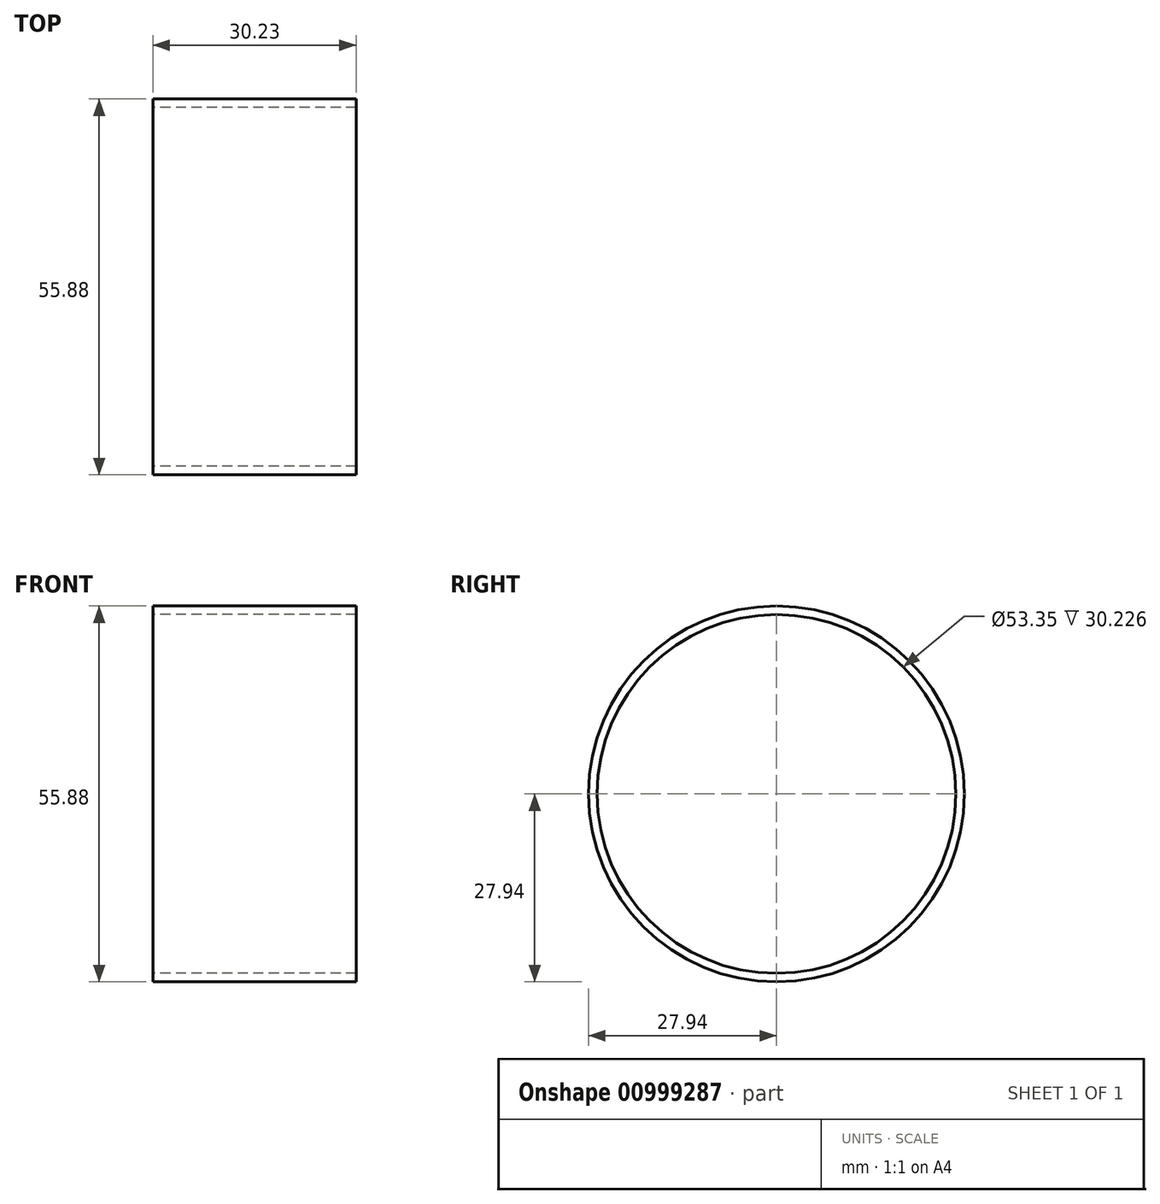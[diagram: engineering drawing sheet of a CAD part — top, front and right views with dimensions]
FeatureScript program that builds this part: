
annotation { "Feature Type Name" : "Feature", "Feature Type Description" : "" }
export const myFeature = defineFeature(function(context is Context, id is Id, definition is map)
    precondition{}
    {
        {
            var Q0;
            Q0=qCreatedBy(makeId("Front.planeOp"),FACE);
            var sketch = newSketch(context, id + "F0", { "sketchPlane" : qUnion([Q0])});
            skLineSegment(sketch, "E0", {"start": v(-34.3, 0) * mm, "end": v(49.05, 0) * mm, "construction": true});
            skLineSegment(sketch, "E1.bottom", {"start": v(-36.86, 27.94) * mm, "end": v(-6.63, 27.94) * mm});
            skLineSegment(sketch, "E1.top", {"start": v(-36.86, 26.67) * mm, "end": v(-6.63, 26.67) * mm});
            skLineSegment(sketch, "E1.left", {"start": v(-36.86, 27.94) * mm, "end": v(-36.86, 26.67) * mm});
            skLineSegment(sketch, "E1.right", {"start": v(-6.63, 27.94) * mm, "end": v(-6.63, 26.67) * mm});
            skSolve(sketch);
        }
        {
            var Q0;
            Q0 = qSketchRegion(id + "F0", true);
            var Q1;
            Q1=sQuery(id+"F0.wireOp",EDGE,"E0");
            revolve(context, id + "F1", {"surfaceOperationType" : NewSurfaceOperationType.NEW, "entities" : qUnion([Q0]), "axis" : qUnion([Q1]), "revolveType" : RevolveType.FULL});
        }
    });
